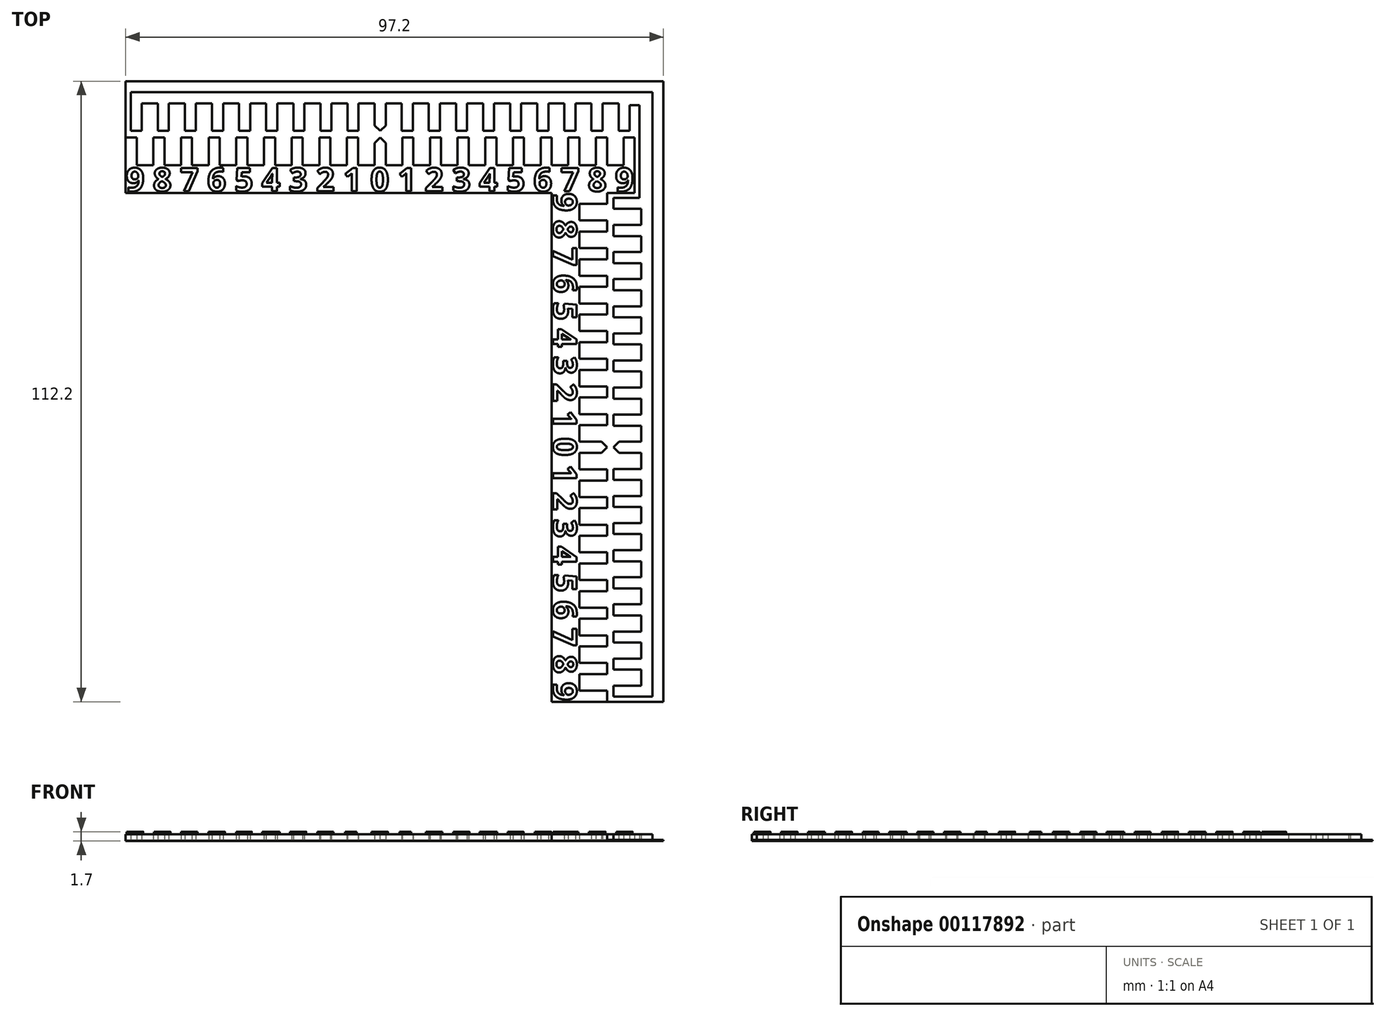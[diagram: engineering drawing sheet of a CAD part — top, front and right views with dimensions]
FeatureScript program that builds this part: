
annotation { "Feature Type Name" : "Feature", "Feature Type Description" : "" }
export const myFeature = defineFeature(function(context is Context, id is Id, definition is map)
    precondition{}
    {
        {
            var Q0;
            Q0=qCreatedBy(makeId("Top.planeOp"),FACE);
            var sketch = newSketch(context, id + "F0", { "sketchPlane" : qUnion([Q0])});
            skLineSegment(sketch, "E0.bottom", {"start": v(-1, 5) * mm, "end": v(1, 5) * mm});
            skLineSegment(sketch, "E0.top", {"start": v(-1, 0) * mm, "end": v(1, 0) * mm});
            skLineSegment(sketch, "E0.left", {"start": v(-1, 5) * mm, "end": v(-1, 0) * mm});
            skLineSegment(sketch, "E0.right", {"start": v(1, 5) * mm, "end": v(1, 0) * mm});
            skLineSegment(sketch, "E1.1.0.0", {"start": v(4, 0) * mm, "end": v(6, 0) * mm});
            skLineSegment(sketch, "E1.1.0.1", {"start": v(4, 5) * mm, "end": v(4, 0) * mm});
            skLineSegment(sketch, "E1.1.0.2", {"start": v(6, 5) * mm, "end": v(6, 0) * mm});
            skLineSegment(sketch, "E1.1.0.3", {"start": v(4, 5) * mm, "end": v(6, 5) * mm});
            skLineSegment(sketch, "E1.2.0.0", {"start": v(9, 0) * mm, "end": v(11, 0) * mm});
            skLineSegment(sketch, "E1.2.0.1", {"start": v(9, 5) * mm, "end": v(9, 0) * mm});
            skLineSegment(sketch, "E1.2.0.2", {"start": v(11, 5) * mm, "end": v(11, 0) * mm});
            skLineSegment(sketch, "E1.2.0.3", {"start": v(9, 5) * mm, "end": v(11, 5) * mm});
            skLineSegment(sketch, "E1.3.0.0", {"start": v(14, 0) * mm, "end": v(16, 0) * mm});
            skLineSegment(sketch, "E1.3.0.1", {"start": v(14, 5) * mm, "end": v(14, 0) * mm});
            skLineSegment(sketch, "E1.3.0.2", {"start": v(16, 5) * mm, "end": v(16, 0) * mm});
            skLineSegment(sketch, "E1.3.0.3", {"start": v(14, 5) * mm, "end": v(16, 5) * mm});
            skLineSegment(sketch, "E1.4.0.0", {"start": v(19, 0) * mm, "end": v(21, 0) * mm});
            skLineSegment(sketch, "E1.4.0.1", {"start": v(19, 5) * mm, "end": v(19, 0) * mm});
            skLineSegment(sketch, "E1.4.0.2", {"start": v(21, 5) * mm, "end": v(21, 0) * mm});
            skLineSegment(sketch, "E1.4.0.3", {"start": v(19, 5) * mm, "end": v(21, 5) * mm});
            skLineSegment(sketch, "E1.5.0.0", {"start": v(24, 0) * mm, "end": v(26, 0) * mm});
            skLineSegment(sketch, "E1.5.0.1", {"start": v(24, 5) * mm, "end": v(24, 0) * mm});
            skLineSegment(sketch, "E1.5.0.2", {"start": v(26, 5) * mm, "end": v(26, 0) * mm});
            skLineSegment(sketch, "E1.5.0.3", {"start": v(24, 5) * mm, "end": v(26, 5) * mm});
            skLineSegment(sketch, "E1.6.0.0", {"start": v(29, 0) * mm, "end": v(31, 0) * mm});
            skLineSegment(sketch, "E1.6.0.1", {"start": v(29, 5) * mm, "end": v(29, 0) * mm});
            skLineSegment(sketch, "E1.6.0.2", {"start": v(31, 5) * mm, "end": v(31, 0) * mm});
            skLineSegment(sketch, "E1.6.0.3", {"start": v(29, 5) * mm, "end": v(31, 5) * mm});
            skLineSegment(sketch, "E1.7.0.0", {"start": v(34, 0) * mm, "end": v(36, 0) * mm});
            skLineSegment(sketch, "E1.7.0.1", {"start": v(34, 5) * mm, "end": v(34, 0) * mm});
            skLineSegment(sketch, "E1.7.0.2", {"start": v(36, 5) * mm, "end": v(36, 0) * mm});
            skLineSegment(sketch, "E1.7.0.3", {"start": v(34, 5) * mm, "end": v(36, 5) * mm});
            skLineSegment(sketch, "E1.8.0.0", {"start": v(39, 0) * mm, "end": v(41, 0) * mm});
            skLineSegment(sketch, "E1.8.0.1", {"start": v(39, 5) * mm, "end": v(39, 0) * mm});
            skLineSegment(sketch, "E1.8.0.2", {"start": v(41, 5) * mm, "end": v(41, 0) * mm});
            skLineSegment(sketch, "E1.8.0.3", {"start": v(39, 5) * mm, "end": v(41, 5) * mm});
            skLineSegment(sketch, "E1.9.0.0", {"start": v(44, 0) * mm, "end": v(46, 0) * mm});
            skLineSegment(sketch, "E1.9.0.1", {"start": v(44, 5) * mm, "end": v(44, 0) * mm});
            skLineSegment(sketch, "E1.9.0.2", {"start": v(46, 5) * mm, "end": v(46, 0) * mm});
            skLineSegment(sketch, "E1.9.0.3", {"start": v(44, 5) * mm, "end": v(46, 5) * mm});
            skLineSegment(sketch, "E1.direction1", {"start": v(-1, 0) * mm, "end": v(4, 0) * mm, "construction": true});
            skLineSegment(sketch, "E2.1.0.0", {"start": v(-4, 5) * mm, "end": v(-4, 0) * mm});
            skLineSegment(sketch, "E2.1.0.1", {"start": v(-6, 5) * mm, "end": v(-6, 0) * mm});
            skLineSegment(sketch, "E2.1.0.2", {"start": v(-6, 0) * mm, "end": v(-4, 0) * mm});
            skLineSegment(sketch, "E2.1.0.3", {"start": v(-6, 5) * mm, "end": v(-4, 5) * mm});
            skLineSegment(sketch, "E2.2.0.0", {"start": v(-9, 5) * mm, "end": v(-9, 0) * mm});
            skLineSegment(sketch, "E2.2.0.1", {"start": v(-11, 5) * mm, "end": v(-11, 0) * mm});
            skLineSegment(sketch, "E2.2.0.2", {"start": v(-11, 0) * mm, "end": v(-9, 0) * mm});
            skLineSegment(sketch, "E2.2.0.3", {"start": v(-11, 5) * mm, "end": v(-9, 5) * mm});
            skLineSegment(sketch, "E2.3.0.0", {"start": v(-14, 5) * mm, "end": v(-14, 0) * mm});
            skLineSegment(sketch, "E2.3.0.1", {"start": v(-16, 5) * mm, "end": v(-16, 0) * mm});
            skLineSegment(sketch, "E2.3.0.2", {"start": v(-16, 0) * mm, "end": v(-14, 0) * mm});
            skLineSegment(sketch, "E2.3.0.3", {"start": v(-16, 5) * mm, "end": v(-14, 5) * mm});
            skLineSegment(sketch, "E2.4.0.0", {"start": v(-19, 5) * mm, "end": v(-19, 0) * mm});
            skLineSegment(sketch, "E2.4.0.1", {"start": v(-21, 5) * mm, "end": v(-21, 0) * mm});
            skLineSegment(sketch, "E2.4.0.2", {"start": v(-21, 0) * mm, "end": v(-19, 0) * mm});
            skLineSegment(sketch, "E2.4.0.3", {"start": v(-21, 5) * mm, "end": v(-19, 5) * mm});
            skLineSegment(sketch, "E2.5.0.0", {"start": v(-24, 5) * mm, "end": v(-24, 0) * mm});
            skLineSegment(sketch, "E2.5.0.1", {"start": v(-26, 5) * mm, "end": v(-26, 0) * mm});
            skLineSegment(sketch, "E2.5.0.2", {"start": v(-26, 0) * mm, "end": v(-24, 0) * mm});
            skLineSegment(sketch, "E2.5.0.3", {"start": v(-26, 5) * mm, "end": v(-24, 5) * mm});
            skLineSegment(sketch, "E2.6.0.0", {"start": v(-29, 5) * mm, "end": v(-29, 0) * mm});
            skLineSegment(sketch, "E2.6.0.1", {"start": v(-31, 5) * mm, "end": v(-31, 0) * mm});
            skLineSegment(sketch, "E2.6.0.2", {"start": v(-31, 0) * mm, "end": v(-29, 0) * mm});
            skLineSegment(sketch, "E2.6.0.3", {"start": v(-31, 5) * mm, "end": v(-29, 5) * mm});
            skLineSegment(sketch, "E2.7.0.0", {"start": v(-34, 5) * mm, "end": v(-34, 0) * mm});
            skLineSegment(sketch, "E2.7.0.1", {"start": v(-36, 5) * mm, "end": v(-36, 0) * mm});
            skLineSegment(sketch, "E2.7.0.2", {"start": v(-36, 0) * mm, "end": v(-34, 0) * mm});
            skLineSegment(sketch, "E2.7.0.3", {"start": v(-36, 5) * mm, "end": v(-34, 5) * mm});
            skLineSegment(sketch, "E2.8.0.0", {"start": v(-39, 5) * mm, "end": v(-39, 0) * mm});
            skLineSegment(sketch, "E2.8.0.1", {"start": v(-41, 5) * mm, "end": v(-41, 0) * mm});
            skLineSegment(sketch, "E2.8.0.2", {"start": v(-41, 0) * mm, "end": v(-39, 0) * mm});
            skLineSegment(sketch, "E2.8.0.3", {"start": v(-41, 5) * mm, "end": v(-39, 5) * mm});
            skLineSegment(sketch, "E2.9.0.0", {"start": v(-44, 5) * mm, "end": v(-44, 0) * mm});
            skLineSegment(sketch, "E2.9.0.1", {"start": v(-46, 5) * mm, "end": v(-46, 0) * mm});
            skLineSegment(sketch, "E2.9.0.2", {"start": v(-46, 0) * mm, "end": v(-44, 0) * mm});
            skLineSegment(sketch, "E2.9.0.3", {"start": v(-46, 5) * mm, "end": v(-44, 5) * mm});
            skLineSegment(sketch, "E2.direction1", {"start": v(-1, 0) * mm, "end": v(-6, 0) * mm, "construction": true});
            skLineSegment(sketch, "E3.bottom", {"start": v(-46, 0) * mm, "end": v(46, 0) * mm});
            skLineSegment(sketch, "E3.top", {"start": v(-46, -5) * mm, "end": v(46, -5) * mm});
            skLineSegment(sketch, "E3.left", {"start": v(-46, 0) * mm, "end": v(-46, -5) * mm});
            skLineSegment(sketch, "E3.right", {"start": v(46, 0) * mm, "end": v(46, -5) * mm});
            skSolve(sketch);
        }
        {
            var Q0;
            Q0 = qSketchRegion(id + "F0", true);
            extrude(context, id + "F1", {"entities" : qUnion([Q0]), "depth" : 1 * mm});
        }
        {
            var Q0;
            Q0=qCreatedBy(makeId("Top.planeOp"),FACE);
            var sketch = newSketch(context, id + "F2", { "sketchPlane" : qUnion([Q0])});
            skLineSegment(sketch, "E4.bottom", {"start": v(-1, -6.2) * mm, "end": v(1, -6.2) * mm});
            skLineSegment(sketch, "E4.top", {"start": v(-1, -11.2) * mm, "end": v(1, -11.2) * mm});
            skLineSegment(sketch, "E4.left", {"start": v(-1, -6.2) * mm, "end": v(-1, -11.2) * mm});
            skLineSegment(sketch, "E4.right", {"start": v(1, -6.2) * mm, "end": v(1, -11.2) * mm});
            skLineSegment(sketch, "E5.1.0.0", {"start": v(3.9, -11.2) * mm, "end": v(5.9, -11.2) * mm});
            skLineSegment(sketch, "E5.1.0.1", {"start": v(3.9, -6.2) * mm, "end": v(3.9, -11.2) * mm});
            skLineSegment(sketch, "E5.1.0.2", {"start": v(5.9, -6.2) * mm, "end": v(5.9, -11.2) * mm});
            skLineSegment(sketch, "E5.1.0.3", {"start": v(3.9, -6.2) * mm, "end": v(5.9, -6.2) * mm});
            skLineSegment(sketch, "E5.2.0.0", {"start": v(8.8, -11.2) * mm, "end": v(10.8, -11.2) * mm});
            skLineSegment(sketch, "E5.2.0.1", {"start": v(8.8, -6.2) * mm, "end": v(8.8, -11.2) * mm});
            skLineSegment(sketch, "E5.2.0.2", {"start": v(10.8, -6.2) * mm, "end": v(10.8, -11.2) * mm});
            skLineSegment(sketch, "E5.2.0.3", {"start": v(8.8, -6.2) * mm, "end": v(10.8, -6.2) * mm});
            skLineSegment(sketch, "E5.3.0.0", {"start": v(13.7, -11.2) * mm, "end": v(15.7, -11.2) * mm});
            skLineSegment(sketch, "E5.3.0.1", {"start": v(13.7, -6.2) * mm, "end": v(13.7, -11.2) * mm});
            skLineSegment(sketch, "E5.3.0.2", {"start": v(15.7, -6.2) * mm, "end": v(15.7, -11.2) * mm});
            skLineSegment(sketch, "E5.3.0.3", {"start": v(13.7, -6.2) * mm, "end": v(15.7, -6.2) * mm});
            skLineSegment(sketch, "E5.4.0.0", {"start": v(18.6, -11.2) * mm, "end": v(20.6, -11.2) * mm});
            skLineSegment(sketch, "E5.4.0.1", {"start": v(18.6, -6.2) * mm, "end": v(18.6, -11.2) * mm});
            skLineSegment(sketch, "E5.4.0.2", {"start": v(20.6, -6.2) * mm, "end": v(20.6, -11.2) * mm});
            skLineSegment(sketch, "E5.4.0.3", {"start": v(18.6, -6.2) * mm, "end": v(20.6, -6.2) * mm});
            skLineSegment(sketch, "E5.5.0.0", {"start": v(23.5, -11.2) * mm, "end": v(25.5, -11.2) * mm});
            skLineSegment(sketch, "E5.5.0.1", {"start": v(23.5, -6.2) * mm, "end": v(23.5, -11.2) * mm});
            skLineSegment(sketch, "E5.5.0.2", {"start": v(25.5, -6.2) * mm, "end": v(25.5, -11.2) * mm});
            skLineSegment(sketch, "E5.5.0.3", {"start": v(23.5, -6.2) * mm, "end": v(25.5, -6.2) * mm});
            skLineSegment(sketch, "E5.6.0.0", {"start": v(28.4, -11.2) * mm, "end": v(30.4, -11.2) * mm});
            skLineSegment(sketch, "E5.6.0.1", {"start": v(28.4, -6.2) * mm, "end": v(28.4, -11.2) * mm});
            skLineSegment(sketch, "E5.6.0.2", {"start": v(30.4, -6.2) * mm, "end": v(30.4, -11.2) * mm});
            skLineSegment(sketch, "E5.6.0.3", {"start": v(28.4, -6.2) * mm, "end": v(30.4, -6.2) * mm});
            skLineSegment(sketch, "E5.7.0.0", {"start": v(33.3, -11.2) * mm, "end": v(35.3, -11.2) * mm});
            skLineSegment(sketch, "E5.7.0.1", {"start": v(33.3, -6.2) * mm, "end": v(33.3, -11.2) * mm});
            skLineSegment(sketch, "E5.7.0.2", {"start": v(35.3, -6.2) * mm, "end": v(35.3, -11.2) * mm});
            skLineSegment(sketch, "E5.7.0.3", {"start": v(33.3, -6.2) * mm, "end": v(35.3, -6.2) * mm});
            skLineSegment(sketch, "E5.8.0.0", {"start": v(38.2, -11.2) * mm, "end": v(40.2, -11.2) * mm});
            skLineSegment(sketch, "E5.8.0.1", {"start": v(38.2, -6.2) * mm, "end": v(38.2, -11.2) * mm});
            skLineSegment(sketch, "E5.8.0.2", {"start": v(40.2, -6.2) * mm, "end": v(40.2, -11.2) * mm});
            skLineSegment(sketch, "E5.8.0.3", {"start": v(38.2, -6.2) * mm, "end": v(40.2, -6.2) * mm});
            skLineSegment(sketch, "E5.9.0.0", {"start": v(43.1, -11.2) * mm, "end": v(45.1, -11.2) * mm});
            skLineSegment(sketch, "E5.9.0.1", {"start": v(43.1, -6.2) * mm, "end": v(43.1, -11.2) * mm});
            skLineSegment(sketch, "E5.9.0.2", {"start": v(45.1, -6.2) * mm, "end": v(45.1, -11.2) * mm});
            skLineSegment(sketch, "E5.9.0.3", {"start": v(43.1, -6.2) * mm, "end": v(45.1, -6.2) * mm});
            skLineSegment(sketch, "E5.direction1", {"start": v(-1, -11.2) * mm, "end": v(3.9, -11.2) * mm, "construction": true});
            skLineSegment(sketch, "E6.1.0.0", {"start": v(-3.9, -6.2) * mm, "end": v(-3.9, -11.2) * mm});
            skLineSegment(sketch, "E6.1.0.1", {"start": v(-5.9, -6.2) * mm, "end": v(-5.9, -11.2) * mm});
            skLineSegment(sketch, "E6.1.0.2", {"start": v(-5.9, -11.2) * mm, "end": v(-3.9, -11.2) * mm});
            skLineSegment(sketch, "E6.1.0.3", {"start": v(-5.9, -6.2) * mm, "end": v(-3.9, -6.2) * mm});
            skLineSegment(sketch, "E6.2.0.0", {"start": v(-8.8, -6.2) * mm, "end": v(-8.8, -11.2) * mm});
            skLineSegment(sketch, "E6.2.0.1", {"start": v(-10.8, -6.2) * mm, "end": v(-10.8, -11.2) * mm});
            skLineSegment(sketch, "E6.2.0.2", {"start": v(-10.8, -11.2) * mm, "end": v(-8.8, -11.2) * mm});
            skLineSegment(sketch, "E6.2.0.3", {"start": v(-10.8, -6.2) * mm, "end": v(-8.8, -6.2) * mm});
            skLineSegment(sketch, "E6.3.0.0", {"start": v(-13.7, -6.2) * mm, "end": v(-13.7, -11.2) * mm});
            skLineSegment(sketch, "E6.3.0.1", {"start": v(-15.7, -6.2) * mm, "end": v(-15.7, -11.2) * mm});
            skLineSegment(sketch, "E6.3.0.2", {"start": v(-15.7, -11.2) * mm, "end": v(-13.7, -11.2) * mm});
            skLineSegment(sketch, "E6.3.0.3", {"start": v(-15.7, -6.2) * mm, "end": v(-13.7, -6.2) * mm});
            skLineSegment(sketch, "E6.4.0.0", {"start": v(-18.6, -6.2) * mm, "end": v(-18.6, -11.2) * mm});
            skLineSegment(sketch, "E6.4.0.1", {"start": v(-20.6, -6.2) * mm, "end": v(-20.6, -11.2) * mm});
            skLineSegment(sketch, "E6.4.0.2", {"start": v(-20.6, -11.2) * mm, "end": v(-18.6, -11.2) * mm});
            skLineSegment(sketch, "E6.4.0.3", {"start": v(-20.6, -6.2) * mm, "end": v(-18.6, -6.2) * mm});
            skLineSegment(sketch, "E6.5.0.0", {"start": v(-23.5, -6.2) * mm, "end": v(-23.5, -11.2) * mm});
            skLineSegment(sketch, "E6.5.0.1", {"start": v(-25.5, -6.2) * mm, "end": v(-25.5, -11.2) * mm});
            skLineSegment(sketch, "E6.5.0.2", {"start": v(-25.5, -11.2) * mm, "end": v(-23.5, -11.2) * mm});
            skLineSegment(sketch, "E6.5.0.3", {"start": v(-25.5, -6.2) * mm, "end": v(-23.5, -6.2) * mm});
            skLineSegment(sketch, "E6.6.0.0", {"start": v(-28.4, -6.2) * mm, "end": v(-28.4, -11.2) * mm});
            skLineSegment(sketch, "E6.6.0.1", {"start": v(-30.4, -6.2) * mm, "end": v(-30.4, -11.2) * mm});
            skLineSegment(sketch, "E6.6.0.2", {"start": v(-30.4, -11.2) * mm, "end": v(-28.4, -11.2) * mm});
            skLineSegment(sketch, "E6.6.0.3", {"start": v(-30.4, -6.2) * mm, "end": v(-28.4, -6.2) * mm});
            skLineSegment(sketch, "E6.7.0.0", {"start": v(-33.3, -6.2) * mm, "end": v(-33.3, -11.2) * mm});
            skLineSegment(sketch, "E6.7.0.1", {"start": v(-35.3, -6.2) * mm, "end": v(-35.3, -11.2) * mm});
            skLineSegment(sketch, "E6.7.0.2", {"start": v(-35.3, -11.2) * mm, "end": v(-33.3, -11.2) * mm});
            skLineSegment(sketch, "E6.7.0.3", {"start": v(-35.3, -6.2) * mm, "end": v(-33.3, -6.2) * mm});
            skLineSegment(sketch, "E6.8.0.0", {"start": v(-38.2, -6.2) * mm, "end": v(-38.2, -11.2) * mm});
            skLineSegment(sketch, "E6.8.0.1", {"start": v(-40.2, -6.2) * mm, "end": v(-40.2, -11.2) * mm});
            skLineSegment(sketch, "E6.8.0.2", {"start": v(-40.2, -11.2) * mm, "end": v(-38.2, -11.2) * mm});
            skLineSegment(sketch, "E6.8.0.3", {"start": v(-40.2, -6.2) * mm, "end": v(-38.2, -6.2) * mm});
            skLineSegment(sketch, "E6.9.0.0", {"start": v(-43.1, -6.2) * mm, "end": v(-43.1, -11.2) * mm});
            skLineSegment(sketch, "E6.9.0.1", {"start": v(-45.1, -6.2) * mm, "end": v(-45.1, -11.2) * mm});
            skLineSegment(sketch, "E6.9.0.2", {"start": v(-45.1, -11.2) * mm, "end": v(-43.1, -11.2) * mm});
            skLineSegment(sketch, "E6.9.0.3", {"start": v(-45.1, -6.2) * mm, "end": v(-43.1, -6.2) * mm});
            skLineSegment(sketch, "E6.direction1", {"start": v(-1, -11.2) * mm, "end": v(-5.9, -11.2) * mm, "construction": true});
            skLineSegment(sketch, "E7.bottom", {"start": v(-45.1, -11.2) * mm, "end": v(45.1, -11.2) * mm});
            skLineSegment(sketch, "E7.top", {"start": v(-45.1, -13.2) * mm, "end": v(45.1, -13.2) * mm});
            skLineSegment(sketch, "E7.left", {"start": v(-45.1, -11.2) * mm, "end": v(-45.1, -13.2) * mm});
            skLineSegment(sketch, "E7.right", {"start": v(45.1, -11.2) * mm, "end": v(45.1, -13.2) * mm});
            skPoint(sketch, "E8", {"position": v(0, -6.2) * mm});
            skSolve(sketch);
        }
        {
            var Q0;
            Q0 = qSketchRegion(id + "F2", true);
            extrude(context, id + "F3", {"entities" : qUnion([Q0]), "depth" : 1 * mm});
        }
        {
            var Q0;
            Q0=makeQuery(id+"F3.opExtrude","SWEPT_BODY",BODY,{"disambiguationData":[OSD([sQuery(id+"F2.wireOp",EDGE,"E4.bottom"),sQuery(id+"F2.wireOp",EDGE,"E4.left"),sQuery(id+"F2.wireOp",EDGE,"E4.right"),sQuery(id+"F2.wireOp",EDGE,"E5.1.0.1"),sQuery(id+"F2.wireOp",EDGE,"E5.1.0.2"),sQuery(id+"F2.wireOp",EDGE,"E5.1.0.3"),sQuery(id+"F2.wireOp",EDGE,"E5.2.0.1"),sQuery(id+"F2.wireOp",EDGE,"E5.2.0.2"),sQuery(id+"F2.wireOp",EDGE,"E5.2.0.3"),sQuery(id+"F2.wireOp",EDGE,"E5.3.0.1"),sQuery(id+"F2.wireOp",EDGE,"E5.3.0.2"),sQuery(id+"F2.wireOp",EDGE,"E5.3.0.3"),sQuery(id+"F2.wireOp",EDGE,"E5.4.0.1"),sQuery(id+"F2.wireOp",EDGE,"E5.4.0.2"),sQuery(id+"F2.wireOp",EDGE,"E5.4.0.3"),sQuery(id+"F2.wireOp",EDGE,"E5.5.0.1"),sQuery(id+"F2.wireOp",EDGE,"E5.5.0.2"),sQuery(id+"F2.wireOp",EDGE,"E5.5.0.3"),sQuery(id+"F2.wireOp",EDGE,"E5.6.0.1"),sQuery(id+"F2.wireOp",EDGE,"E5.6.0.2"),sQuery(id+"F2.wireOp",EDGE,"E5.6.0.3"),sQuery(id+"F2.wireOp",EDGE,"E5.7.0.1"),sQuery(id+"F2.wireOp",EDGE,"E5.7.0.2"),sQuery(id+"F2.wireOp",EDGE,"E5.7.0.3"),sQuery(id+"F2.wireOp",EDGE,"E5.8.0.1"),sQuery(id+"F2.wireOp",EDGE,"E5.8.0.2"),sQuery(id+"F2.wireOp",EDGE,"E5.8.0.3"),sQuery(id+"F2.wireOp",EDGE,"E5.9.0.1"),sQuery(id+"F2.wireOp",EDGE,"E5.9.0.2"),sQuery(id+"F2.wireOp",EDGE,"E5.9.0.3"),sQuery(id+"F2.wireOp",EDGE,"E6.1.0.0"),sQuery(id+"F2.wireOp",EDGE,"E6.1.0.1"),sQuery(id+"F2.wireOp",EDGE,"E6.1.0.3"),sQuery(id+"F2.wireOp",EDGE,"E6.2.0.0"),sQuery(id+"F2.wireOp",EDGE,"E6.2.0.1"),sQuery(id+"F2.wireOp",EDGE,"E6.2.0.3"),sQuery(id+"F2.wireOp",EDGE,"E6.3.0.0"),sQuery(id+"F2.wireOp",EDGE,"E6.3.0.1"),sQuery(id+"F2.wireOp",EDGE,"E6.3.0.3"),sQuery(id+"F2.wireOp",EDGE,"E6.4.0.0"),sQuery(id+"F2.wireOp",EDGE,"E6.4.0.1"),sQuery(id+"F2.wireOp",EDGE,"E6.4.0.3"),sQuery(id+"F2.wireOp",EDGE,"E6.5.0.0"),sQuery(id+"F2.wireOp",EDGE,"E6.5.0.1"),sQuery(id+"F2.wireOp",EDGE,"E6.5.0.3"),sQuery(id+"F2.wireOp",EDGE,"E6.6.0.0"),sQuery(id+"F2.wireOp",EDGE,"E6.6.0.1"),sQuery(id+"F2.wireOp",EDGE,"E6.6.0.3"),sQuery(id+"F2.wireOp",EDGE,"E6.7.0.0"),sQuery(id+"F2.wireOp",EDGE,"E6.7.0.1"),sQuery(id+"F2.wireOp",EDGE,"E6.7.0.3"),sQuery(id+"F2.wireOp",EDGE,"E6.8.0.0"),sQuery(id+"F2.wireOp",EDGE,"E6.8.0.1"),sQuery(id+"F2.wireOp",EDGE,"E6.8.0.3"),sQuery(id+"F2.wireOp",EDGE,"E6.9.0.0"),sQuery(id+"F2.wireOp",EDGE,"E6.9.0.1"),sQuery(id+"F2.wireOp",EDGE,"E6.9.0.3"),sQuery(id+"F2.wireOp",EDGE,"E7.bottom"),sQuery(id+"F2.wireOp",EDGE,"E7.top"),sQuery(id+"F2.wireOp",EDGE,"E7.left"),sQuery(id+"F2.wireOp",EDGE,"E7.right")])]});
            var Q1;
            Q1=qCreatedBy(makeId("Front.planeOp"),FACE);
            mirror(context, id + "F4", {"entities" : qUnion([Q0]), "mirrorPlane" : qUnion([Q1])});
        }
        {
            var Q0;
            Q0=makeQuery(id+"F3.opExtrude","SWEPT_BODY",BODY,{"disambiguationData":[OSD([sQuery(id+"F2.wireOp",EDGE,"E4.bottom"),sQuery(id+"F2.wireOp",EDGE,"E4.left"),sQuery(id+"F2.wireOp",EDGE,"E4.right"),sQuery(id+"F2.wireOp",EDGE,"E5.1.0.1"),sQuery(id+"F2.wireOp",EDGE,"E5.1.0.2"),sQuery(id+"F2.wireOp",EDGE,"E5.1.0.3"),sQuery(id+"F2.wireOp",EDGE,"E5.2.0.1"),sQuery(id+"F2.wireOp",EDGE,"E5.2.0.2"),sQuery(id+"F2.wireOp",EDGE,"E5.2.0.3"),sQuery(id+"F2.wireOp",EDGE,"E5.3.0.1"),sQuery(id+"F2.wireOp",EDGE,"E5.3.0.2"),sQuery(id+"F2.wireOp",EDGE,"E5.3.0.3"),sQuery(id+"F2.wireOp",EDGE,"E5.4.0.1"),sQuery(id+"F2.wireOp",EDGE,"E5.4.0.2"),sQuery(id+"F2.wireOp",EDGE,"E5.4.0.3"),sQuery(id+"F2.wireOp",EDGE,"E5.5.0.1"),sQuery(id+"F2.wireOp",EDGE,"E5.5.0.2"),sQuery(id+"F2.wireOp",EDGE,"E5.5.0.3"),sQuery(id+"F2.wireOp",EDGE,"E5.6.0.1"),sQuery(id+"F2.wireOp",EDGE,"E5.6.0.2"),sQuery(id+"F2.wireOp",EDGE,"E5.6.0.3"),sQuery(id+"F2.wireOp",EDGE,"E5.7.0.1"),sQuery(id+"F2.wireOp",EDGE,"E5.7.0.2"),sQuery(id+"F2.wireOp",EDGE,"E5.7.0.3"),sQuery(id+"F2.wireOp",EDGE,"E5.8.0.1"),sQuery(id+"F2.wireOp",EDGE,"E5.8.0.2"),sQuery(id+"F2.wireOp",EDGE,"E5.8.0.3"),sQuery(id+"F2.wireOp",EDGE,"E5.9.0.1"),sQuery(id+"F2.wireOp",EDGE,"E5.9.0.2"),sQuery(id+"F2.wireOp",EDGE,"E5.9.0.3"),sQuery(id+"F2.wireOp",EDGE,"E6.1.0.0"),sQuery(id+"F2.wireOp",EDGE,"E6.1.0.1"),sQuery(id+"F2.wireOp",EDGE,"E6.1.0.3"),sQuery(id+"F2.wireOp",EDGE,"E6.2.0.0"),sQuery(id+"F2.wireOp",EDGE,"E6.2.0.1"),sQuery(id+"F2.wireOp",EDGE,"E6.2.0.3"),sQuery(id+"F2.wireOp",EDGE,"E6.3.0.0"),sQuery(id+"F2.wireOp",EDGE,"E6.3.0.1"),sQuery(id+"F2.wireOp",EDGE,"E6.3.0.3"),sQuery(id+"F2.wireOp",EDGE,"E6.4.0.0"),sQuery(id+"F2.wireOp",EDGE,"E6.4.0.1"),sQuery(id+"F2.wireOp",EDGE,"E6.4.0.3"),sQuery(id+"F2.wireOp",EDGE,"E6.5.0.0"),sQuery(id+"F2.wireOp",EDGE,"E6.5.0.1"),sQuery(id+"F2.wireOp",EDGE,"E6.5.0.3"),sQuery(id+"F2.wireOp",EDGE,"E6.6.0.0"),sQuery(id+"F2.wireOp",EDGE,"E6.6.0.1"),sQuery(id+"F2.wireOp",EDGE,"E6.6.0.3"),sQuery(id+"F2.wireOp",EDGE,"E6.7.0.0"),sQuery(id+"F2.wireOp",EDGE,"E6.7.0.1"),sQuery(id+"F2.wireOp",EDGE,"E6.7.0.3"),sQuery(id+"F2.wireOp",EDGE,"E6.8.0.0"),sQuery(id+"F2.wireOp",EDGE,"E6.8.0.1"),sQuery(id+"F2.wireOp",EDGE,"E6.8.0.3"),sQuery(id+"F2.wireOp",EDGE,"E6.9.0.0"),sQuery(id+"F2.wireOp",EDGE,"E6.9.0.1"),sQuery(id+"F2.wireOp",EDGE,"E6.9.0.3"),sQuery(id+"F2.wireOp",EDGE,"E7.bottom"),sQuery(id+"F2.wireOp",EDGE,"E7.top"),sQuery(id+"F2.wireOp",EDGE,"E7.left"),sQuery(id+"F2.wireOp",EDGE,"E7.right")])]});
            deleteBodies(context, id + "F5", {"entities" : qUnion([Q0])});
        }
        {
            var Q0;
            Q0=makeQuery(id+"F1.opExtrude","CAP_FACE",FACE,{"disambiguationData":[OSD([sQuery(id+"F0.wireOp",EDGE,"E0.bottom"),sQuery(id+"F0.wireOp",EDGE,"E0.left"),sQuery(id+"F0.wireOp",EDGE,"E0.right"),sQuery(id+"F0.wireOp",EDGE,"E1.1.0.1"),sQuery(id+"F0.wireOp",EDGE,"E1.1.0.2"),sQuery(id+"F0.wireOp",EDGE,"E1.1.0.3"),sQuery(id+"F0.wireOp",EDGE,"E1.2.0.1"),sQuery(id+"F0.wireOp",EDGE,"E1.2.0.2"),sQuery(id+"F0.wireOp",EDGE,"E1.2.0.3"),sQuery(id+"F0.wireOp",EDGE,"E1.3.0.1"),sQuery(id+"F0.wireOp",EDGE,"E1.3.0.2"),sQuery(id+"F0.wireOp",EDGE,"E1.3.0.3"),sQuery(id+"F0.wireOp",EDGE,"E1.4.0.1"),sQuery(id+"F0.wireOp",EDGE,"E1.4.0.2"),sQuery(id+"F0.wireOp",EDGE,"E1.4.0.3"),sQuery(id+"F0.wireOp",EDGE,"E1.5.0.1"),sQuery(id+"F0.wireOp",EDGE,"E1.5.0.2"),sQuery(id+"F0.wireOp",EDGE,"E1.5.0.3"),sQuery(id+"F0.wireOp",EDGE,"E1.6.0.1"),sQuery(id+"F0.wireOp",EDGE,"E1.6.0.2"),sQuery(id+"F0.wireOp",EDGE,"E1.6.0.3"),sQuery(id+"F0.wireOp",EDGE,"E1.7.0.1"),sQuery(id+"F0.wireOp",EDGE,"E1.7.0.2"),sQuery(id+"F0.wireOp",EDGE,"E1.7.0.3"),sQuery(id+"F0.wireOp",EDGE,"E1.8.0.1"),sQuery(id+"F0.wireOp",EDGE,"E1.8.0.2"),sQuery(id+"F0.wireOp",EDGE,"E1.8.0.3"),sQuery(id+"F0.wireOp",EDGE,"E1.9.0.1"),sQuery(id+"F0.wireOp",EDGE,"E1.9.0.2"),sQuery(id+"F0.wireOp",EDGE,"E1.9.0.3"),sQuery(id+"F0.wireOp",EDGE,"E2.1.0.0"),sQuery(id+"F0.wireOp",EDGE,"E2.1.0.1"),sQuery(id+"F0.wireOp",EDGE,"E2.1.0.3"),sQuery(id+"F0.wireOp",EDGE,"E2.2.0.0"),sQuery(id+"F0.wireOp",EDGE,"E2.2.0.1"),sQuery(id+"F0.wireOp",EDGE,"E2.2.0.3"),sQuery(id+"F0.wireOp",EDGE,"E2.3.0.0"),sQuery(id+"F0.wireOp",EDGE,"E2.3.0.1"),sQuery(id+"F0.wireOp",EDGE,"E2.3.0.3"),sQuery(id+"F0.wireOp",EDGE,"E2.4.0.0"),sQuery(id+"F0.wireOp",EDGE,"E2.4.0.1"),sQuery(id+"F0.wireOp",EDGE,"E2.4.0.3"),sQuery(id+"F0.wireOp",EDGE,"E2.5.0.0"),sQuery(id+"F0.wireOp",EDGE,"E2.5.0.1"),sQuery(id+"F0.wireOp",EDGE,"E2.5.0.3"),sQuery(id+"F0.wireOp",EDGE,"E2.6.0.0"),sQuery(id+"F0.wireOp",EDGE,"E2.6.0.1"),sQuery(id+"F0.wireOp",EDGE,"E2.6.0.3"),sQuery(id+"F0.wireOp",EDGE,"E2.7.0.0"),sQuery(id+"F0.wireOp",EDGE,"E2.7.0.1"),sQuery(id+"F0.wireOp",EDGE,"E2.7.0.3"),sQuery(id+"F0.wireOp",EDGE,"E2.8.0.0"),sQuery(id+"F0.wireOp",EDGE,"E2.8.0.1"),sQuery(id+"F0.wireOp",EDGE,"E2.8.0.3"),sQuery(id+"F0.wireOp",EDGE,"E2.9.0.0"),sQuery(id+"F0.wireOp",EDGE,"E2.9.0.1"),sQuery(id+"F0.wireOp",EDGE,"E2.9.0.3"),sQuery(id+"F0.wireOp",EDGE,"E3.bottom"),sQuery(id+"F0.wireOp",EDGE,"E3.top"),sQuery(id+"F0.wireOp",EDGE,"E3.left"),sQuery(id+"F0.wireOp",EDGE,"E3.right")])],"isStart":false});
            var sketch = newSketch(context, id + "F6", { "sketchPlane" : qUnion([Q0])});
            skText(sketch, "E9", { "text": "9 8 7 6 5 4 3 2 1 0 1 2 3 4 5 6 7 8 9", "fontName": "OpenSans-Bold.ttf"});
            const initialGuessF6  = {"E9": [-0.046, -0.00472, 1, 0, 0.00426]};
            skSetInitialGuess(sketch, initialGuessF6);
            skSolve(sketch);
        }
        {
            var Q0;
            Q0 = qSketchRegion(id + "F6", true);
            extrude(context, id + "F7", {"entities" : qUnion([Q0]), "operationType" : NewBodyOperationType.ADD, "depth" : .5 * mm});
        }
        {
            var Q0;
            Q0=makeQuery(id+"F4.opPattern","COPY",EDGE,{"derivedFrom":makeQuery(id+"F3.opExtrude","SWEPT_EDGE",EDGE,{"disambiguationData":[OSD([sQuery(id+"F2.wireOp",EDGE,"E4.bottom"),sQuery(id+"F2.wireOp",EDGE,"E4.left")])]}),"instanceName":"1"});
            var Q1;
            Q1=makeQuery(id+"F4.opPattern","COPY",EDGE,{"derivedFrom":makeQuery(id+"F3.opExtrude","SWEPT_EDGE",EDGE,{"disambiguationData":[OSD([sQuery(id+"F2.wireOp",EDGE,"E4.bottom"),sQuery(id+"F2.wireOp",EDGE,"E4.right")])]}),"instanceName":"1"});
            var Q2;
            Q2=makeQuery(id+"F1.opExtrude","SWEPT_EDGE",EDGE,{"disambiguationData":[OSD([sQuery(id+"F0.wireOp",EDGE,"E0.bottom"),sQuery(id+"F0.wireOp",EDGE,"E0.right")])]});
            var Q3;
            Q3=makeQuery(id+"F1.opExtrude","SWEPT_EDGE",EDGE,{"disambiguationData":[OSD([sQuery(id+"F0.wireOp",EDGE,"E0.bottom"),sQuery(id+"F0.wireOp",EDGE,"E0.left")])]});
            chamfer(context, id + "F8", {"entities" : qUnion([Q0, Q1, Q2, Q3]), "width" : 1 * mm, "tangentPropagation" : true});
        }
        {
            var Q0;
            Q0=makeQuery(id+"F1.opExtrude","SWEPT_BODY",BODY,{"disambiguationData":[OSD([sQuery(id+"F0.wireOp",EDGE,"E0.bottom"),sQuery(id+"F0.wireOp",EDGE,"E0.left"),sQuery(id+"F0.wireOp",EDGE,"E0.right"),sQuery(id+"F0.wireOp",EDGE,"E1.1.0.1"),sQuery(id+"F0.wireOp",EDGE,"E1.1.0.2"),sQuery(id+"F0.wireOp",EDGE,"E1.1.0.3"),sQuery(id+"F0.wireOp",EDGE,"E1.2.0.1"),sQuery(id+"F0.wireOp",EDGE,"E1.2.0.2"),sQuery(id+"F0.wireOp",EDGE,"E1.2.0.3"),sQuery(id+"F0.wireOp",EDGE,"E1.3.0.1"),sQuery(id+"F0.wireOp",EDGE,"E1.3.0.2"),sQuery(id+"F0.wireOp",EDGE,"E1.3.0.3"),sQuery(id+"F0.wireOp",EDGE,"E1.4.0.1"),sQuery(id+"F0.wireOp",EDGE,"E1.4.0.2"),sQuery(id+"F0.wireOp",EDGE,"E1.4.0.3"),sQuery(id+"F0.wireOp",EDGE,"E1.5.0.1"),sQuery(id+"F0.wireOp",EDGE,"E1.5.0.2"),sQuery(id+"F0.wireOp",EDGE,"E1.5.0.3"),sQuery(id+"F0.wireOp",EDGE,"E1.6.0.1"),sQuery(id+"F0.wireOp",EDGE,"E1.6.0.2"),sQuery(id+"F0.wireOp",EDGE,"E1.6.0.3"),sQuery(id+"F0.wireOp",EDGE,"E1.7.0.1"),sQuery(id+"F0.wireOp",EDGE,"E1.7.0.2"),sQuery(id+"F0.wireOp",EDGE,"E1.7.0.3"),sQuery(id+"F0.wireOp",EDGE,"E1.8.0.1"),sQuery(id+"F0.wireOp",EDGE,"E1.8.0.2"),sQuery(id+"F0.wireOp",EDGE,"E1.8.0.3"),sQuery(id+"F0.wireOp",EDGE,"E1.9.0.1"),sQuery(id+"F0.wireOp",EDGE,"E1.9.0.2"),sQuery(id+"F0.wireOp",EDGE,"E1.9.0.3"),sQuery(id+"F0.wireOp",EDGE,"E2.1.0.0"),sQuery(id+"F0.wireOp",EDGE,"E2.1.0.1"),sQuery(id+"F0.wireOp",EDGE,"E2.1.0.3"),sQuery(id+"F0.wireOp",EDGE,"E2.2.0.0"),sQuery(id+"F0.wireOp",EDGE,"E2.2.0.1"),sQuery(id+"F0.wireOp",EDGE,"E2.2.0.3"),sQuery(id+"F0.wireOp",EDGE,"E2.3.0.0"),sQuery(id+"F0.wireOp",EDGE,"E2.3.0.1"),sQuery(id+"F0.wireOp",EDGE,"E2.3.0.3"),sQuery(id+"F0.wireOp",EDGE,"E2.4.0.0"),sQuery(id+"F0.wireOp",EDGE,"E2.4.0.1"),sQuery(id+"F0.wireOp",EDGE,"E2.4.0.3"),sQuery(id+"F0.wireOp",EDGE,"E2.5.0.0"),sQuery(id+"F0.wireOp",EDGE,"E2.5.0.1"),sQuery(id+"F0.wireOp",EDGE,"E2.5.0.3"),sQuery(id+"F0.wireOp",EDGE,"E2.6.0.0"),sQuery(id+"F0.wireOp",EDGE,"E2.6.0.1"),sQuery(id+"F0.wireOp",EDGE,"E2.6.0.3"),sQuery(id+"F0.wireOp",EDGE,"E2.7.0.0"),sQuery(id+"F0.wireOp",EDGE,"E2.7.0.1"),sQuery(id+"F0.wireOp",EDGE,"E2.7.0.3"),sQuery(id+"F0.wireOp",EDGE,"E2.8.0.0"),sQuery(id+"F0.wireOp",EDGE,"E2.8.0.1"),sQuery(id+"F0.wireOp",EDGE,"E2.8.0.3"),sQuery(id+"F0.wireOp",EDGE,"E2.9.0.0"),sQuery(id+"F0.wireOp",EDGE,"E2.9.0.1"),sQuery(id+"F0.wireOp",EDGE,"E2.9.0.3"),sQuery(id+"F0.wireOp",EDGE,"E3.bottom"),sQuery(id+"F0.wireOp",EDGE,"E3.top"),sQuery(id+"F0.wireOp",EDGE,"E3.left"),sQuery(id+"F0.wireOp",EDGE,"E3.right")])]});
            var Q1;
            Q1=makeQuery(id+"F1.opExtrude","SWEPT_EDGE",EDGE,{"disambiguationData":[OSD([sQuery(id+"F0.wireOp",EDGE,"E3.top"),sQuery(id+"F0.wireOp",EDGE,"E3.left")])]});
            transform(context, id + "F9", {"entities" : qUnion([Q0]), "transformType" : TransformType.ROTATION, "transformAxis" : qUnion([Q1]), "angle" : 90 * degree, "makeCopy" : true});
        }
        {
            var Q0;
            Q0=makeQuery(id+"F4.opPattern","COPY",BODY,{"derivedFrom":makeQuery(id+"F3.opExtrude","SWEPT_BODY",BODY,{"disambiguationData":[OSD([sQuery(id+"F2.wireOp",EDGE,"E4.bottom"),sQuery(id+"F2.wireOp",EDGE,"E4.left"),sQuery(id+"F2.wireOp",EDGE,"E4.right"),sQuery(id+"F2.wireOp",EDGE,"E5.1.0.1"),sQuery(id+"F2.wireOp",EDGE,"E5.1.0.2"),sQuery(id+"F2.wireOp",EDGE,"E5.1.0.3"),sQuery(id+"F2.wireOp",EDGE,"E5.2.0.1"),sQuery(id+"F2.wireOp",EDGE,"E5.2.0.2"),sQuery(id+"F2.wireOp",EDGE,"E5.2.0.3"),sQuery(id+"F2.wireOp",EDGE,"E5.3.0.1"),sQuery(id+"F2.wireOp",EDGE,"E5.3.0.2"),sQuery(id+"F2.wireOp",EDGE,"E5.3.0.3"),sQuery(id+"F2.wireOp",EDGE,"E5.4.0.1"),sQuery(id+"F2.wireOp",EDGE,"E5.4.0.2"),sQuery(id+"F2.wireOp",EDGE,"E5.4.0.3"),sQuery(id+"F2.wireOp",EDGE,"E5.5.0.1"),sQuery(id+"F2.wireOp",EDGE,"E5.5.0.2"),sQuery(id+"F2.wireOp",EDGE,"E5.5.0.3"),sQuery(id+"F2.wireOp",EDGE,"E5.6.0.1"),sQuery(id+"F2.wireOp",EDGE,"E5.6.0.2"),sQuery(id+"F2.wireOp",EDGE,"E5.6.0.3"),sQuery(id+"F2.wireOp",EDGE,"E5.7.0.1"),sQuery(id+"F2.wireOp",EDGE,"E5.7.0.2"),sQuery(id+"F2.wireOp",EDGE,"E5.7.0.3"),sQuery(id+"F2.wireOp",EDGE,"E5.8.0.1"),sQuery(id+"F2.wireOp",EDGE,"E5.8.0.2"),sQuery(id+"F2.wireOp",EDGE,"E5.8.0.3"),sQuery(id+"F2.wireOp",EDGE,"E5.9.0.1"),sQuery(id+"F2.wireOp",EDGE,"E5.9.0.2"),sQuery(id+"F2.wireOp",EDGE,"E5.9.0.3"),sQuery(id+"F2.wireOp",EDGE,"E6.1.0.0"),sQuery(id+"F2.wireOp",EDGE,"E6.1.0.1"),sQuery(id+"F2.wireOp",EDGE,"E6.1.0.3"),sQuery(id+"F2.wireOp",EDGE,"E6.2.0.0"),sQuery(id+"F2.wireOp",EDGE,"E6.2.0.1"),sQuery(id+"F2.wireOp",EDGE,"E6.2.0.3"),sQuery(id+"F2.wireOp",EDGE,"E6.3.0.0"),sQuery(id+"F2.wireOp",EDGE,"E6.3.0.1"),sQuery(id+"F2.wireOp",EDGE,"E6.3.0.3"),sQuery(id+"F2.wireOp",EDGE,"E6.4.0.0"),sQuery(id+"F2.wireOp",EDGE,"E6.4.0.1"),sQuery(id+"F2.wireOp",EDGE,"E6.4.0.3"),sQuery(id+"F2.wireOp",EDGE,"E6.5.0.0"),sQuery(id+"F2.wireOp",EDGE,"E6.5.0.1"),sQuery(id+"F2.wireOp",EDGE,"E6.5.0.3"),sQuery(id+"F2.wireOp",EDGE,"E6.6.0.0"),sQuery(id+"F2.wireOp",EDGE,"E6.6.0.1"),sQuery(id+"F2.wireOp",EDGE,"E6.6.0.3"),sQuery(id+"F2.wireOp",EDGE,"E6.7.0.0"),sQuery(id+"F2.wireOp",EDGE,"E6.7.0.1"),sQuery(id+"F2.wireOp",EDGE,"E6.7.0.3"),sQuery(id+"F2.wireOp",EDGE,"E6.8.0.0"),sQuery(id+"F2.wireOp",EDGE,"E6.8.0.1"),sQuery(id+"F2.wireOp",EDGE,"E6.8.0.3"),sQuery(id+"F2.wireOp",EDGE,"E6.9.0.0"),sQuery(id+"F2.wireOp",EDGE,"E6.9.0.1"),sQuery(id+"F2.wireOp",EDGE,"E6.9.0.3"),sQuery(id+"F2.wireOp",EDGE,"E7.bottom"),sQuery(id+"F2.wireOp",EDGE,"E7.top"),sQuery(id+"F2.wireOp",EDGE,"E7.left"),sQuery(id+"F2.wireOp",EDGE,"E7.right")])]}),"instanceName":"1"});
            var Q1;
            Q1=makeQuery(id+"F1.opExtrude","SWEPT_EDGE",EDGE,{"disambiguationData":[OSD([sQuery(id+"F0.wireOp",EDGE,"E3.top"),sQuery(id+"F0.wireOp",EDGE,"E3.left")])]});
            transform(context, id + "F10", {"entities" : qUnion([Q0]), "transformType" : TransformType.ROTATION, "transformAxis" : qUnion([Q1]), "angle" : 90 * degree, "makeCopy" : true});
        }
        {
            var Q0;
            Q0=makeQuery(id+"F9.opPattern","COPY",BODY,{"derivedFrom":makeQuery(id+"F1.opExtrude","SWEPT_BODY",BODY,{"disambiguationData":[OSD([sQuery(id+"F0.wireOp",EDGE,"E0.bottom"),sQuery(id+"F0.wireOp",EDGE,"E0.left"),sQuery(id+"F0.wireOp",EDGE,"E0.right"),sQuery(id+"F0.wireOp",EDGE,"E1.1.0.1"),sQuery(id+"F0.wireOp",EDGE,"E1.1.0.2"),sQuery(id+"F0.wireOp",EDGE,"E1.1.0.3"),sQuery(id+"F0.wireOp",EDGE,"E1.2.0.1"),sQuery(id+"F0.wireOp",EDGE,"E1.2.0.2"),sQuery(id+"F0.wireOp",EDGE,"E1.2.0.3"),sQuery(id+"F0.wireOp",EDGE,"E1.3.0.1"),sQuery(id+"F0.wireOp",EDGE,"E1.3.0.2"),sQuery(id+"F0.wireOp",EDGE,"E1.3.0.3"),sQuery(id+"F0.wireOp",EDGE,"E1.4.0.1"),sQuery(id+"F0.wireOp",EDGE,"E1.4.0.2"),sQuery(id+"F0.wireOp",EDGE,"E1.4.0.3"),sQuery(id+"F0.wireOp",EDGE,"E1.5.0.1"),sQuery(id+"F0.wireOp",EDGE,"E1.5.0.2"),sQuery(id+"F0.wireOp",EDGE,"E1.5.0.3"),sQuery(id+"F0.wireOp",EDGE,"E1.6.0.1"),sQuery(id+"F0.wireOp",EDGE,"E1.6.0.2"),sQuery(id+"F0.wireOp",EDGE,"E1.6.0.3"),sQuery(id+"F0.wireOp",EDGE,"E1.7.0.1"),sQuery(id+"F0.wireOp",EDGE,"E1.7.0.2"),sQuery(id+"F0.wireOp",EDGE,"E1.7.0.3"),sQuery(id+"F0.wireOp",EDGE,"E1.8.0.1"),sQuery(id+"F0.wireOp",EDGE,"E1.8.0.2"),sQuery(id+"F0.wireOp",EDGE,"E1.8.0.3"),sQuery(id+"F0.wireOp",EDGE,"E1.9.0.1"),sQuery(id+"F0.wireOp",EDGE,"E1.9.0.2"),sQuery(id+"F0.wireOp",EDGE,"E1.9.0.3"),sQuery(id+"F0.wireOp",EDGE,"E2.1.0.0"),sQuery(id+"F0.wireOp",EDGE,"E2.1.0.1"),sQuery(id+"F0.wireOp",EDGE,"E2.1.0.3"),sQuery(id+"F0.wireOp",EDGE,"E2.2.0.0"),sQuery(id+"F0.wireOp",EDGE,"E2.2.0.1"),sQuery(id+"F0.wireOp",EDGE,"E2.2.0.3"),sQuery(id+"F0.wireOp",EDGE,"E2.3.0.0"),sQuery(id+"F0.wireOp",EDGE,"E2.3.0.1"),sQuery(id+"F0.wireOp",EDGE,"E2.3.0.3"),sQuery(id+"F0.wireOp",EDGE,"E2.4.0.0"),sQuery(id+"F0.wireOp",EDGE,"E2.4.0.1"),sQuery(id+"F0.wireOp",EDGE,"E2.4.0.3"),sQuery(id+"F0.wireOp",EDGE,"E2.5.0.0"),sQuery(id+"F0.wireOp",EDGE,"E2.5.0.1"),sQuery(id+"F0.wireOp",EDGE,"E2.5.0.3"),sQuery(id+"F0.wireOp",EDGE,"E2.6.0.0"),sQuery(id+"F0.wireOp",EDGE,"E2.6.0.1"),sQuery(id+"F0.wireOp",EDGE,"E2.6.0.3"),sQuery(id+"F0.wireOp",EDGE,"E2.7.0.0"),sQuery(id+"F0.wireOp",EDGE,"E2.7.0.1"),sQuery(id+"F0.wireOp",EDGE,"E2.7.0.3"),sQuery(id+"F0.wireOp",EDGE,"E2.8.0.0"),sQuery(id+"F0.wireOp",EDGE,"E2.8.0.1"),sQuery(id+"F0.wireOp",EDGE,"E2.8.0.3"),sQuery(id+"F0.wireOp",EDGE,"E2.9.0.0"),sQuery(id+"F0.wireOp",EDGE,"E2.9.0.1"),sQuery(id+"F0.wireOp",EDGE,"E2.9.0.3"),sQuery(id+"F0.wireOp",EDGE,"E3.bottom"),sQuery(id+"F0.wireOp",EDGE,"E3.top"),sQuery(id+"F0.wireOp",EDGE,"E3.left"),sQuery(id+"F0.wireOp",EDGE,"E3.right")])]}),"instanceName":"1"});
            var Q1;
            Q1=makeQuery(id+"F10.opPattern","COPY",BODY,{"derivedFrom":makeQuery(id+"F4.opPattern","COPY",BODY,{"derivedFrom":makeQuery(id+"F3.opExtrude","SWEPT_BODY",BODY,{"disambiguationData":[OSD([sQuery(id+"F2.wireOp",EDGE,"E4.bottom"),sQuery(id+"F2.wireOp",EDGE,"E4.left"),sQuery(id+"F2.wireOp",EDGE,"E4.right"),sQuery(id+"F2.wireOp",EDGE,"E5.1.0.1"),sQuery(id+"F2.wireOp",EDGE,"E5.1.0.2"),sQuery(id+"F2.wireOp",EDGE,"E5.1.0.3"),sQuery(id+"F2.wireOp",EDGE,"E5.2.0.1"),sQuery(id+"F2.wireOp",EDGE,"E5.2.0.2"),sQuery(id+"F2.wireOp",EDGE,"E5.2.0.3"),sQuery(id+"F2.wireOp",EDGE,"E5.3.0.1"),sQuery(id+"F2.wireOp",EDGE,"E5.3.0.2"),sQuery(id+"F2.wireOp",EDGE,"E5.3.0.3"),sQuery(id+"F2.wireOp",EDGE,"E5.4.0.1"),sQuery(id+"F2.wireOp",EDGE,"E5.4.0.2"),sQuery(id+"F2.wireOp",EDGE,"E5.4.0.3"),sQuery(id+"F2.wireOp",EDGE,"E5.5.0.1"),sQuery(id+"F2.wireOp",EDGE,"E5.5.0.2"),sQuery(id+"F2.wireOp",EDGE,"E5.5.0.3"),sQuery(id+"F2.wireOp",EDGE,"E5.6.0.1"),sQuery(id+"F2.wireOp",EDGE,"E5.6.0.2"),sQuery(id+"F2.wireOp",EDGE,"E5.6.0.3"),sQuery(id+"F2.wireOp",EDGE,"E5.7.0.1"),sQuery(id+"F2.wireOp",EDGE,"E5.7.0.2"),sQuery(id+"F2.wireOp",EDGE,"E5.7.0.3"),sQuery(id+"F2.wireOp",EDGE,"E5.8.0.1"),sQuery(id+"F2.wireOp",EDGE,"E5.8.0.2"),sQuery(id+"F2.wireOp",EDGE,"E5.8.0.3"),sQuery(id+"F2.wireOp",EDGE,"E5.9.0.1"),sQuery(id+"F2.wireOp",EDGE,"E5.9.0.2"),sQuery(id+"F2.wireOp",EDGE,"E5.9.0.3"),sQuery(id+"F2.wireOp",EDGE,"E6.1.0.0"),sQuery(id+"F2.wireOp",EDGE,"E6.1.0.1"),sQuery(id+"F2.wireOp",EDGE,"E6.1.0.3"),sQuery(id+"F2.wireOp",EDGE,"E6.2.0.0"),sQuery(id+"F2.wireOp",EDGE,"E6.2.0.1"),sQuery(id+"F2.wireOp",EDGE,"E6.2.0.3"),sQuery(id+"F2.wireOp",EDGE,"E6.3.0.0"),sQuery(id+"F2.wireOp",EDGE,"E6.3.0.1"),sQuery(id+"F2.wireOp",EDGE,"E6.3.0.3"),sQuery(id+"F2.wireOp",EDGE,"E6.4.0.0"),sQuery(id+"F2.wireOp",EDGE,"E6.4.0.1"),sQuery(id+"F2.wireOp",EDGE,"E6.4.0.3"),sQuery(id+"F2.wireOp",EDGE,"E6.5.0.0"),sQuery(id+"F2.wireOp",EDGE,"E6.5.0.1"),sQuery(id+"F2.wireOp",EDGE,"E6.5.0.3"),sQuery(id+"F2.wireOp",EDGE,"E6.6.0.0"),sQuery(id+"F2.wireOp",EDGE,"E6.6.0.1"),sQuery(id+"F2.wireOp",EDGE,"E6.6.0.3"),sQuery(id+"F2.wireOp",EDGE,"E6.7.0.0"),sQuery(id+"F2.wireOp",EDGE,"E6.7.0.1"),sQuery(id+"F2.wireOp",EDGE,"E6.7.0.3"),sQuery(id+"F2.wireOp",EDGE,"E6.8.0.0"),sQuery(id+"F2.wireOp",EDGE,"E6.8.0.1"),sQuery(id+"F2.wireOp",EDGE,"E6.8.0.3"),sQuery(id+"F2.wireOp",EDGE,"E6.9.0.0"),sQuery(id+"F2.wireOp",EDGE,"E6.9.0.1"),sQuery(id+"F2.wireOp",EDGE,"E6.9.0.3"),sQuery(id+"F2.wireOp",EDGE,"E7.bottom"),sQuery(id+"F2.wireOp",EDGE,"E7.top"),sQuery(id+"F2.wireOp",EDGE,"E7.left"),sQuery(id+"F2.wireOp",EDGE,"E7.right")])]}),"instanceName":"1"}),"instanceName":"1"});
            var Q2;
            Q2=makeQuery(id+"F1.opExtrude","CAP_EDGE",EDGE,{"disambiguationData":[OSD([sQuery(id+"F0.wireOp",EDGE,"E3.top")])],"isStart":true});
            var Q3;
            Q3=qCreatedBy(makeId("Right.planeOp"),FACE);
            transform(context, id + "F11", {"entities" : qUnion([Q0, Q1]), "transformType" : TransformType.TRANSLATION_DISTANCE, "transformDirection" : qUnion([Q3]), "distance" : 77 * mm, "makeCopy" : false});
        }
        {
            var Q0;
            Q0=qCreatedBy(makeId("Top.planeOp"),FACE);
            var sketch = newSketch(context, id + "F12", { "sketchPlane" : qUnion([Q0])});
            skLineSegment(sketch, "E10", {"start": v(49.2, -5.9) * mm, "end": v(49.2, 13.2) * mm});
            skLineSegment(sketch, "E11", {"start": v(49.2, 13.2) * mm, "end": v(45.1, 13.2) * mm});
            skLineSegment(sketch, "E12", {"start": v(45.1, 13.2) * mm, "end": v(45.1, 10.85) * mm});
            skLineSegment(sketch, "E13", {"start": v(45.1, 10.85) * mm, "end": v(46.85, 10.85) * mm});
            skLineSegment(sketch, "E14", {"start": v(46.85, 10.85) * mm, "end": v(46.85, -5.9) * mm});
            skLineSegment(sketch, "E15", {"start": v(46.85, -5.9) * mm, "end": v(49.2, -5.9) * mm});
            skSolve(sketch);
        }
        {
            var Q0;
            Q0 = qSketchRegion(id + "F12", true);
            extrude(context, id + "F13", {"entities" : qUnion([Q0]), "operationType" : NewBodyOperationType.ADD, "depth" : 1 * mm});
        }
        {
            var Q0;
            Q0=qCreatedBy(makeId("Top.planeOp"),FACE);
            var sketch = newSketch(context, id + "F14", { "sketchPlane" : qUnion([Q0])});
            skLineSegment(sketch, "E16", {"start": v(-46, -5) * mm, "end": v(-46, 15.2) * mm});
            skLineSegment(sketch, "E17", {"start": v(-46, 15.2) * mm, "end": v(51.2, 15.2) * mm});
            skLineSegment(sketch, "E18", {"start": v(51.2, 15.2) * mm, "end": v(51.2, -97) * mm});
            skLineSegment(sketch, "E19", {"start": v(51.2, -97) * mm, "end": v(31, -97) * mm});
            skLineSegment(sketch, "E20", {"start": v(31, -97) * mm, "end": v(31, -5) * mm});
            skLineSegment(sketch, "E21", {"start": v(31, -5) * mm, "end": v(-46, -5) * mm});
            skSolve(sketch);
        }
        {
            var Q0;
            Q0 = qSketchRegion(id + "F14", true);
            extrude(context, id + "F15", {"entities" : qUnion([Q0]), "operationType" : NewBodyOperationType.ADD, "oppositeDirection" : true, "depth" : 0.2 * mm});
        }
    });
